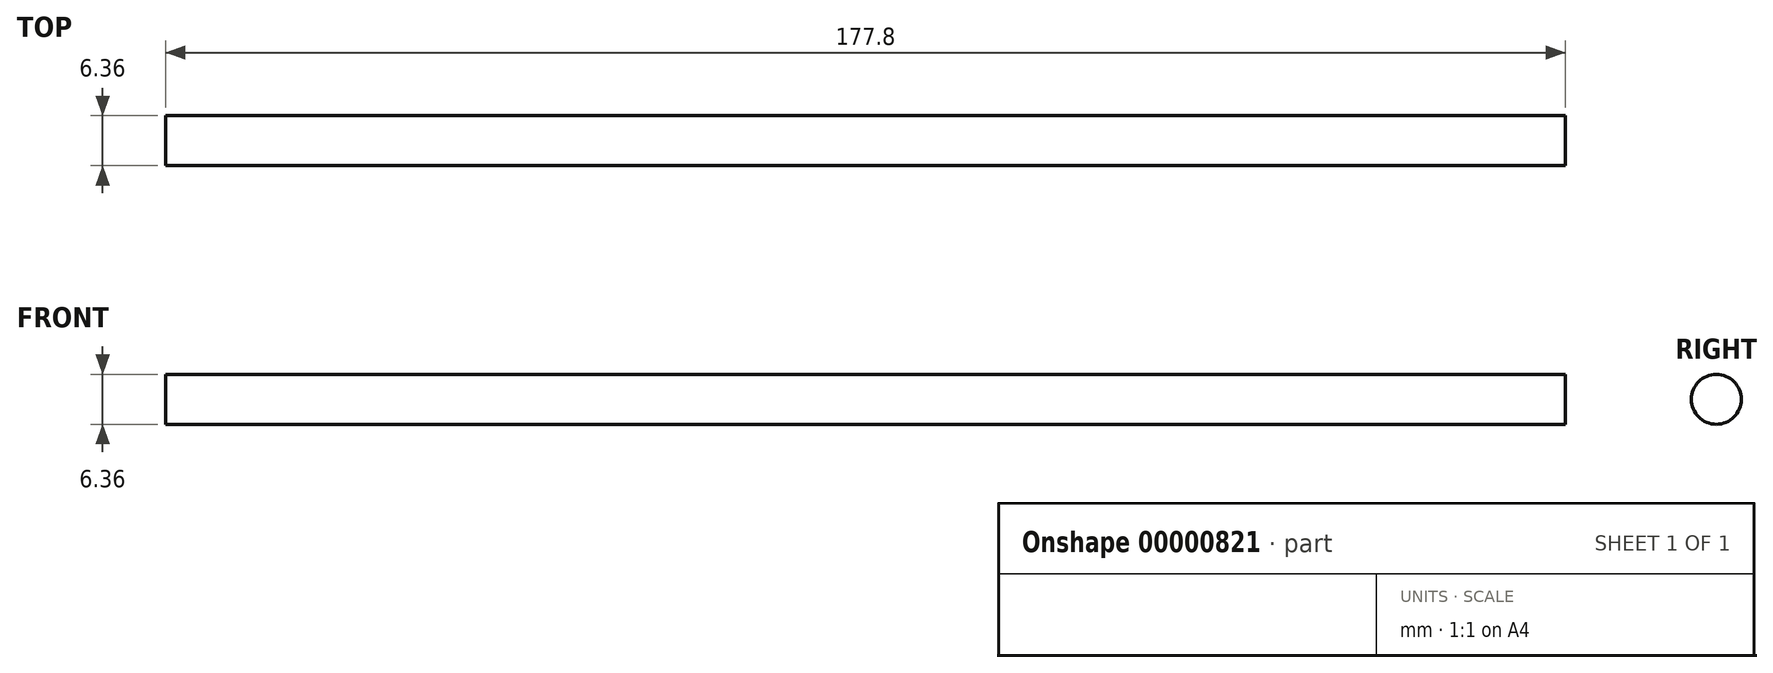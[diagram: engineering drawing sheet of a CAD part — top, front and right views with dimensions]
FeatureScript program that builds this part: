
annotation { "Feature Type Name" : "Feature", "Feature Type Description" : "" }
export const myFeature = defineFeature(function(context is Context, id is Id, definition is map)
    precondition{}
    {
        {
            var Q0;
            Q0=qCreatedBy(makeId("Right.planeOp"),FACE);
            var sketch = newSketch(context, id + "F0", { "sketchPlane" : qUnion([Q0])});
            skCircle(sketch, "E0", {"center": v(0, 0) * mm, "radius": 3.18 * mm});
            skSolve(sketch);
        }
        {
            var Q0;
            Q0=makeQuery(id+"F0.imprint","IMPRINT",FACE,{"disambiguationData":[TD([[makeQuery(id+"F0.imprint","IMPRINT",EDGE,{"derivedFrom":sQuery(id+"F0.wireOp",EDGE,"E0")}),1.0]])]});
            extrude(context, id + "F1", {"entities" : qUnion([Q0]), "endBound" : BoundingType.SYMMETRIC, "depth" : 177.8 * mm});
        }
    });
